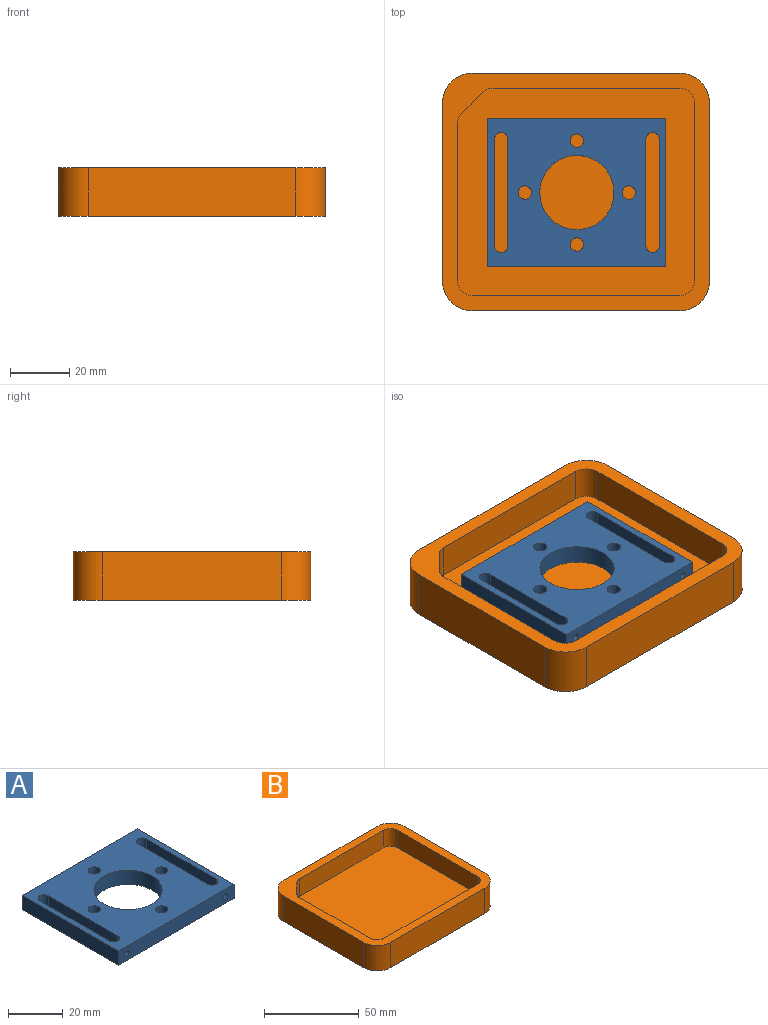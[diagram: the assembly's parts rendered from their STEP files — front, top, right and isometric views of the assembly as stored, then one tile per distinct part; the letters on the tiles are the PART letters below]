
ASSEMBLY  parts=2 mates=1
PART A: 21 faces, bbox 60x50x6.4 mm
  f0: cylinder r=2.25mm len=6.35mm, axis (0,0,-1), area 39.8mm2, adj f5,f15,f17,f18,f20
  f1: cylinder r=2.25mm len=6.35mm, axis (0,0,-1), area 39.8mm2, adj f2,f4,f17,f18,f19
  f2: plane 36x6.35mm, normal (1,0,0), area 228.6mm2, adj f1,f3,f17,f18
  f3: cylinder r=2.25mm len=6.35mm, axis (0,0,-1), area 44.9mm2, adj f2,f4,f17,f18
  f4: plane 36x6.35mm, normal (-1,0,0), area 228.6mm2, adj f1,f3,f17,f18
  f5: plane 36x6.35mm, normal (1,0,0), area 228.6mm2, adj f0,f6,f17,f18
  f6: cylinder r=2.25mm len=6.35mm, axis (0,0,-1), area 44.9mm2, adj f5,f15,f17,f18
  f7: plane 50x6.35mm, normal (1,0,0), area 317.5mm2, adj f8,f16,f17,f18
  f8: plane 60x6.35mm, normal (0,1,0), area 381mm2, adj f7,f9,f17,f18
  f9: plane 50x6.35mm, normal (-1,0,0), area 317.5mm2, adj f8,f16,f17,f18
  f10: cylinder r=2.25mm len=6.35mm, axis (0,0,-1), area 89.8mm2, adj f17,f18
  f11: cylinder r=2.25mm len=6.35mm, axis (0,0,-1), area 89.8mm2, adj f17,f18
  f12: cylinder r=2.25mm len=6.35mm, axis (0,0,-1), area 89.8mm2, adj f17,f18
  f13: cylinder r=2.25mm len=6.35mm, axis (0,0,-1), area 89.8mm2, adj f17,f18
  f14: cylinder r=12.5mm len=25mm, axis (0,0,-1), area 498.7mm2, adj f17,f18
  f15: plane 36x6.35mm, normal (-1,0,0), area 228.6mm2, adj f0,f6,f17,f18
  f16: plane 60x6.35mm, normal (0,-1,0), area 371.2mm2, adj f7,f9,f17,f18,f19,f20
  f17: plane 60x50mm, normal (0,0,1), area 2089.7mm2, adj f0,f1,f2,f3,f4,f5,f6,f7
  f18: plane 60x50mm, normal (0,0,-1), area 2089.7mm2, adj f0,f1,f2,f3,f4,f5,f6,f7
  f19: cylinder r=1.25mm len=5.13mm, axis (0,-1,0), area 38.8mm2, adj f1,f16
  f20: cylinder r=1.25mm len=5.13mm, axis (0,-1,0), area 38.8mm2, adj f0,f16
PART B: 21 faces, bbox 90x80x16.4 mm
  f0: cylinder r=5mm len=11.35mm, axis (0,0,-1), area 89.1mm2, adj f1,f17,f18,f20
  f1: plane 59.88x11.35mm, normal (-1,0,0), area 679.6mm2, adj f0,f2,f18,f20
  f2: cylinder r=5mm len=11.35mm, axis (0,0,-1), area 89.1mm2, adj f1,f3,f18,f20
  f3: plane 70x11.35mm, normal (0,1,0), area 794.5mm2, adj f2,f4,f18,f20
  f4: cylinder r=5mm len=11.35mm, axis (0,0,-1), area 89.1mm2, adj f3,f5,f18,f20
  f5: plane 52.8x11.35mm, normal (1,0,0), area 599.3mm2, adj f4,f6,f18,f20
  f6: cylinder r=5mm len=11.35mm, axis (0,0,-1), area 44.6mm2, adj f5,f7,f18,f20
  f7: plane 11.35x7.07mm, normal (0.71,-0.71,0), area 113.5mm2, adj f6,f8,f18,f20
  f8: cylinder r=5mm len=11.35mm, axis (0,0,-1), area 44.6mm2, adj f7,f17,f18,f20
  f9: plane 60x16.35mm, normal (1,0,0), area 981mm2, adj f10,f16,f18,f19
  f10: cylinder r=10mm len=16.35mm, axis (0,0,-1), area 256.8mm2, adj f9,f11,f18,f19
  f11: plane 70x16.35mm, normal (0,1,0), area 1144.5mm2, adj f10,f12,f18,f19
  f12: cylinder r=10mm len=16.35mm, axis (0,0,-1), area 256.8mm2, adj f11,f13,f18,f19
  f13: plane 60x16.35mm, normal (-1,0,0), area 981mm2, adj f12,f14,f18,f19
  f14: cylinder r=10mm len=16.35mm, axis (0,0,-1), area 256.8mm2, adj f13,f15,f18,f19
  f15: plane 70x16.35mm, normal (0,-1,0), area 1144.5mm2, adj f14,f16,f18,f19
  f16: cylinder r=10mm len=16.35mm, axis (0,0,-1), area 256.8mm2, adj f9,f15,f18,f19
  f17: plane 62.93x11.35mm, normal (0,-1,0), area 714.2mm2, adj f0,f8,f18,f20
  f18: plane 90x80mm, normal (0,0,1), area 1591.3mm2, adj f0,f1,f2,f3,f4,f5,f6,f7
  f19: plane 90x80mm, normal (0,0,-1), area 7114.2mm2, adj f9,f10,f11,f12,f13,f14,f15,f16
  f20: plane 80x69.88mm, normal (0,0,1), area 5522.8mm2, adj f0,f1,f2,f3,f4,f5,f6,f7
PLACE A at identity
PLACE B t=(-0.3,0.32,-5)mm
MATE fastened A.f14 <-> B.f20  axis (0,0,1) through (0,0,0)mm
